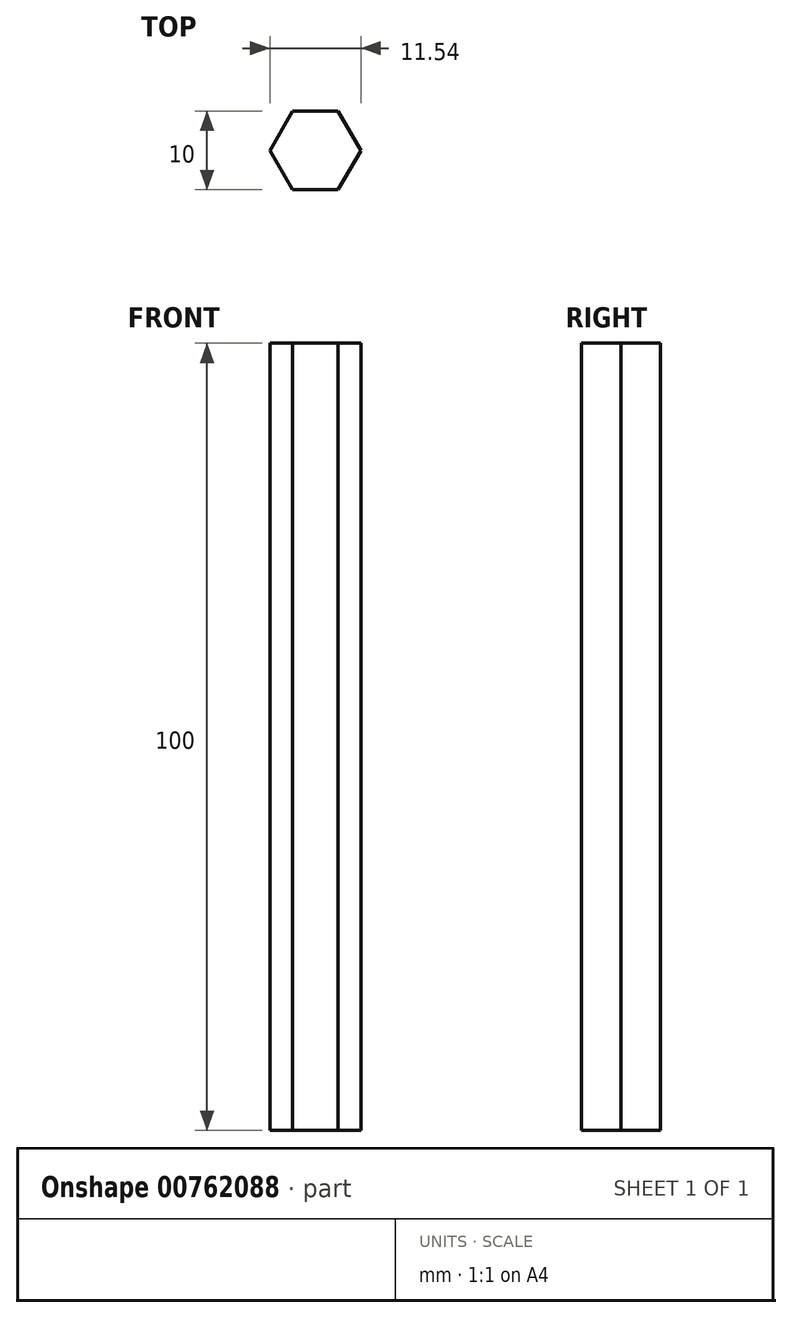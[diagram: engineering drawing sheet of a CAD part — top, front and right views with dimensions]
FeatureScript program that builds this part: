
annotation { "Feature Type Name" : "Feature", "Feature Type Description" : "" }
export const myFeature = defineFeature(function(context is Context, id is Id, definition is map)
    precondition{}
    {
        {
            var Q0;
            Q0=qCreatedBy(makeId("Top.planeOp"),FACE);
            var sketch = newSketch(context, id + "F0", { "sketchPlane" : qUnion([Q0])});
            skCircle(sketch, "E0.cCircle", {"center": v(0, 0) * mm, "radius": 5 * mm, "construction": true});
            skLineSegment(sketch, "E0.0", {"start": v(-2.89, 5) * mm, "end": v(2.89, 5) * mm});
            skLineSegment(sketch, "E0.1", {"start": v(2.89, 5) * mm, "end": v(5.77, 0) * mm});
            skLineSegment(sketch, "E0.2", {"start": v(5.77, 0) * mm, "end": v(2.89, -5) * mm});
            skLineSegment(sketch, "E0.3", {"start": v(2.89, -5) * mm, "end": v(-2.89, -5) * mm});
            skLineSegment(sketch, "E0.4", {"start": v(-2.89, -5) * mm, "end": v(-5.77, 0) * mm});
            skLineSegment(sketch, "E0.5", {"start": v(-5.77, 0) * mm, "end": v(-2.89, 5) * mm});
            skPoint(sketch, "E0.0.midPoint", {"position": v(0, 5) * mm});
            skSolve(sketch);
        }
        {
            var Q0;
            Q0 = qSketchRegion(id + "F0", true);
            extrude(context, id + "F1", {"entities" : qUnion([Q0]), "depth" : 100 * mm, "offsetDistance" : 25 * mm});
        }
    });
